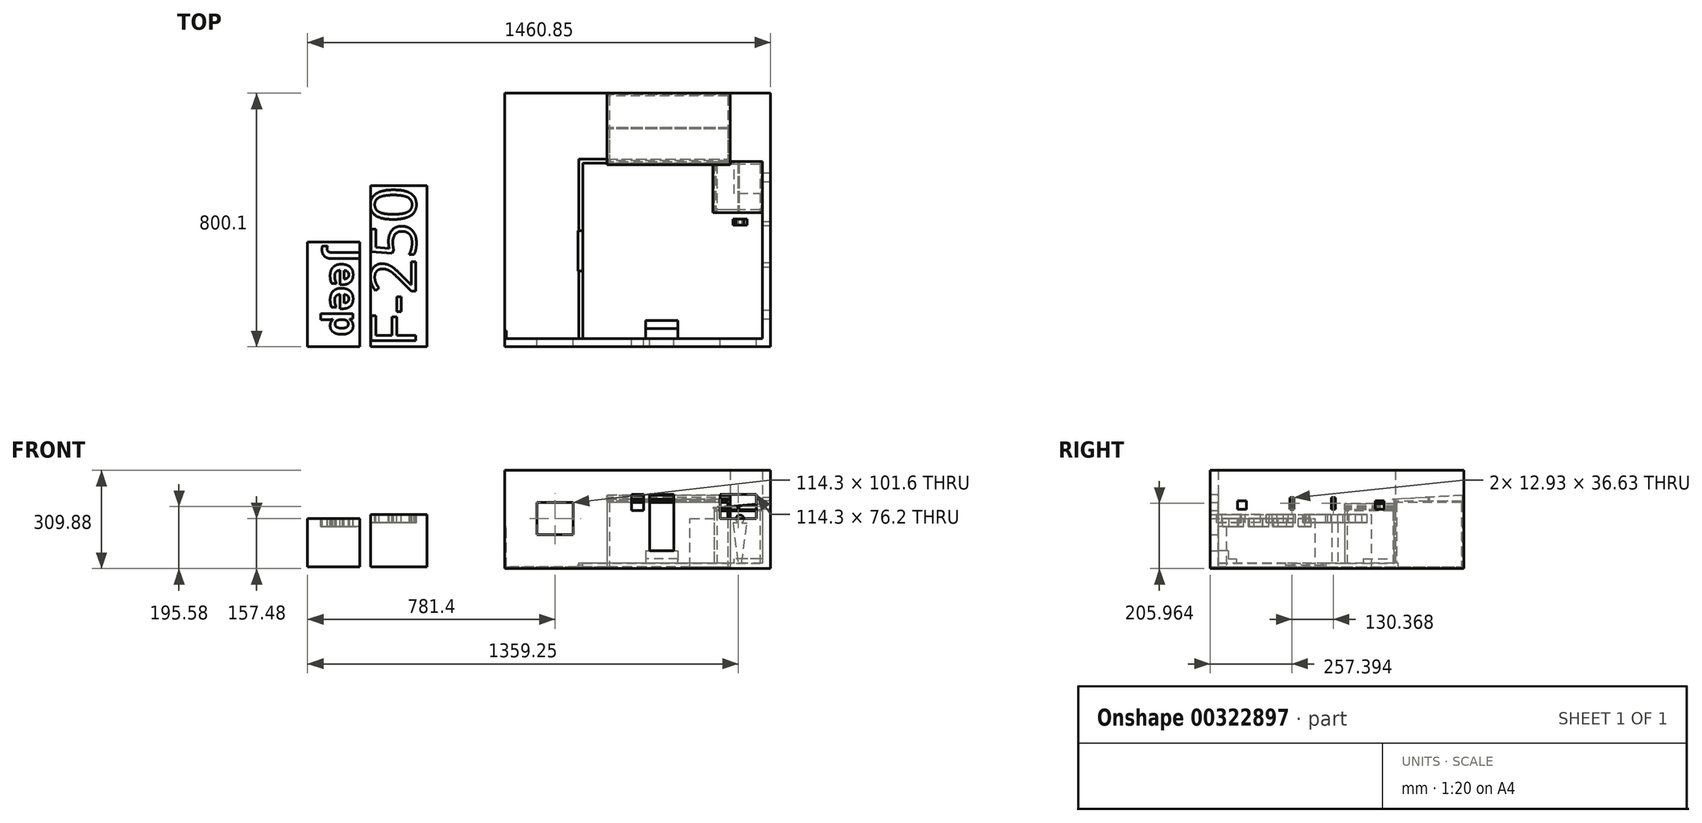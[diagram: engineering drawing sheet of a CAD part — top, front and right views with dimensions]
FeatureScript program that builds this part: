
annotation { "Feature Type Name" : "Feature", "Feature Type Description" : "" }
export const myFeature = defineFeature(function(context is Context, id is Id, definition is map)
    precondition{}
    {
        {
            var Q0;
            Q0=qCreatedBy(makeId("Top.planeOp"),FACE);
            var sketch = newSketch(context, id + "F0", { "sketchPlane" : qUnion([Q0])});
            skLineSegment(sketch, "E0.bottom", {"start": v(0, 0) * mm, "end": v(146.74, 0) * mm});
            skLineSegment(sketch, "E0.top", {"start": v(25.4, 25.4) * mm, "end": v(812.8, 25.4) * mm});
            skLineSegment(sketch, "E0.left", {"start": v(0, 0) * mm, "end": v(0, 25.4) * mm});
            skLineSegment(sketch, "E1.right", {"start": v(838.2, 25.4) * mm, "end": v(838.2, 584.2) * mm});
            skLineSegment(sketch, "E2", {"start": v(0, 25.4) * mm, "end": v(25.4, 25.4) * mm});
            skLineSegment(sketch, "E3", {"start": v(146.74, 0) * mm, "end": v(838.2, 0) * mm});
            skLineSegment(sketch, "E4", {"start": v(838.2, 0) * mm, "end": v(838.2, 25.4) * mm});
            skLineSegment(sketch, "E5.left", {"start": v(838.2, 584.2) * mm, "end": v(838.2, 192.84) * mm});
            skLineSegment(sketch, "E5.right", {"start": v(812.8, 584.2) * mm, "end": v(812.8, 25.4) * mm});
            skLineSegment(sketch, "E6.bottom", {"start": v(812.8, 584.2) * mm, "end": v(711.2, 584.2) * mm});
            skLineSegment(sketch, "E6.top", {"start": v(838.2, 800.1) * mm, "end": v(711.2, 800.1) * mm});
            skLineSegment(sketch, "E6.left", {"start": v(838.2, 584.2) * mm, "end": v(838.2, 800.1) * mm});
            skLineSegment(sketch, "E6.right", {"start": v(711.2, 584.2) * mm, "end": v(711.2, 800.1) * mm});
            skSolve(sketch);
        }
        {
            var Q0;
            Q0 = qSketchRegion(id + "F0", true);
            extrude(context, id + "F1", {"entities" : qUnion([Q0]), "depth" : 304.8 * mm});
        }
        {
            var Q0;
            Q0=makeQuery(id+"F1.opExtrude","SWEPT_FACE",FACE,{"disambiguationData":[OSD([sQuery(id+"F0.wireOp",EDGE,"E6.right")])]});
            var sketch = newSketch(context, id + "F2", { "sketchPlane" : qUnion([Q0])});
            skLineSegment(sketch, "E7.bottom", {"start": v(-800.1, 0) * mm, "end": v(-795.02, 0) * mm});
            skLineSegment(sketch, "E7.top", {"start": v(-800.1, 152.4) * mm, "end": v(-795.02, 152.4) * mm});
            skLineSegment(sketch, "E7.left", {"start": v(-800.1, 0) * mm, "end": v(-800.1, 152.4) * mm});
            skLineSegment(sketch, "E7.right", {"start": v(-795.02, 0) * mm, "end": v(-795.02, 152.4) * mm});
            skSolve(sketch);
        }
        {
            var Q0;
            Q0 = qSketchRegion(id + "F2", true);
            extrude(context, id + "F3", {"entities" : qUnion([Q0]), "operationType" : NewBodyOperationType.ADD, "depth" : 127 * mm});
        }
        {
            var Q0;
            Q0=makeQuery(id+"F1.opExtrude","SWEPT_FACE",FACE,{"disambiguationData":[OSD([sQuery(id+"F0.wireOp",EDGE,"E0.top"),sQuery(id+"F0.wireOp",EDGE,"E2")])]});
            var sketch = newSketch(context, id + "F4", { "sketchPlane" : qUnion([Q0])});
            skLineSegment(sketch, "E8.bottom", {"start": v(-101.6, 101.6) * mm, "end": v(-215.9, 101.6) * mm});
            skLineSegment(sketch, "E8.top", {"start": v(-101.6, 203.2) * mm, "end": v(-215.9, 203.2) * mm});
            skLineSegment(sketch, "E8.left", {"start": v(-101.6, 101.6) * mm, "end": v(-101.6, 203.2) * mm});
            skLineSegment(sketch, "E8.right", {"start": v(-215.9, 101.6) * mm, "end": v(-215.9, 203.2) * mm});
            skLineSegment(sketch, "E9.bottom", {"start": v(-400.05, 177.8) * mm, "end": v(-438.15, 177.8) * mm});
            skLineSegment(sketch, "E9.top", {"start": v(-400.05, 228.6) * mm, "end": v(-438.15, 228.6) * mm});
            skLineSegment(sketch, "E9.left", {"start": v(-400.05, 177.8) * mm, "end": v(-400.05, 228.6) * mm});
            skLineSegment(sketch, "E9.right", {"start": v(-438.15, 177.8) * mm, "end": v(-438.15, 228.6) * mm});
            skLineSegment(sketch, "E10.bottom", {"start": v(-679.45, 228.6) * mm, "end": v(-793.75, 228.6) * mm});
            skLineSegment(sketch, "E10.top", {"start": v(-679.45, 152.4) * mm, "end": v(-793.75, 152.4) * mm});
            skLineSegment(sketch, "E10.left", {"start": v(-679.45, 228.6) * mm, "end": v(-679.45, 152.4) * mm});
            skLineSegment(sketch, "E10.right", {"start": v(-793.75, 228.6) * mm, "end": v(-793.75, 152.4) * mm});
            skLineSegment(sketch, "E11.bottom", {"start": v(-457.2, 228.6) * mm, "end": v(-533.4, 228.6) * mm});
            skLineSegment(sketch, "E11.top", {"start": v(-457.2, 50.8) * mm, "end": v(-533.4, 50.8) * mm});
            skLineSegment(sketch, "E11.left", {"start": v(-457.2, 228.6) * mm, "end": v(-457.2, 50.8) * mm});
            skLineSegment(sketch, "E11.right", {"start": v(-533.4, 228.6) * mm, "end": v(-533.4, 50.8) * mm});
            skSolve(sketch);
        }
        {
            var Q0;
            Q0 = qSketchRegion(id + "F4", true);
            extrude(context, id + "F5", {"entities" : qUnion([Q0]), "operationType" : NewBodyOperationType.REMOVE, "endBound" : BoundingType.UP_TO_NEXT, "oppositeDirection" : true, "depth" : 25.4 * mm});
        }
        {
            var Q0;
            Q0=makeQuery(id+"F1.opExtrude","SWEPT_FACE",FACE,{"disambiguationData":[OSD([sQuery(id+"F0.wireOp",EDGE,"E0.top"),sQuery(id+"F0.wireOp",EDGE,"E2")])]});
            var sketch = newSketch(context, id + "F6", { "sketchPlane" : qUnion([Q0])});
            skLineSegment(sketch, "E12.bottom", {"start": v(-444.5, 50.8) * mm, "end": v(-546.1, 50.8) * mm});
            skLineSegment(sketch, "E12.top", {"start": v(-444.5, 0) * mm, "end": v(-546.1, 0) * mm});
            skLineSegment(sketch, "E12.left", {"start": v(-444.5, 50.8) * mm, "end": v(-444.5, 0) * mm});
            skLineSegment(sketch, "E12.right", {"start": v(-546.1, 50.8) * mm, "end": v(-546.1, 0) * mm});
            skSolve(sketch);
        }
        {
            var Q0;
            Q0 = qSketchRegion(id + "F6", true);
            extrude(context, id + "F7", {"entities" : qUnion([Q0]), "operationType" : NewBodyOperationType.ADD, "depth" : 31.75 * mm});
        }
        {
            var Q0;
            Q0=makeQuery(id+"F7.opExtrude","SWEPT_FACE",FACE,{"disambiguationData":[OSD([sQuery(id+"F6.wireOp",EDGE,"E12.left")])]});
            var sketch = newSketch(context, id + "F8", { "sketchPlane" : qUnion([Q0])});
            skLineSegment(sketch, "E13.bottom", {"start": v(-57.15, 25.4) * mm, "end": v(-82.55, 25.4) * mm});
            skLineSegment(sketch, "E13.top", {"start": v(-57.15, 0) * mm, "end": v(-82.55, 0) * mm});
            skLineSegment(sketch, "E13.left", {"start": v(-57.15, 25.4) * mm, "end": v(-57.15, 0) * mm});
            skLineSegment(sketch, "E13.right", {"start": v(-82.55, 25.4) * mm, "end": v(-82.55, 0) * mm});
            skSolve(sketch);
        }
        {
            var Q0;
            Q0 = qSketchRegion(id + "F8", true);
            var Q1;
            Q1=makeQuery(id+"F7.opExtrude","SWEPT_FACE",FACE,{"disambiguationData":[OSD([sQuery(id+"F6.wireOp",EDGE,"E12.right")])]});
            extrude(context, id + "F9", {"entities" : qUnion([Q0]), "operationType" : NewBodyOperationType.ADD, "endBound" : BoundingType.UP_TO_SURFACE, "oppositeDirection" : true, "endBoundEntityFace" : qUnion([Q1]), "depth" : 25.4 * mm});
        }
        {
            var Q0;
            Q0=makeQuery(id+"F1.opExtrude","SWEPT_FACE",FACE,{"disambiguationData":[OSD([sQuery(id+"F0.wireOp",EDGE,"E0.top"),sQuery(id+"F0.wireOp",EDGE,"E2")])]});
            var sketch = newSketch(context, id + "F10", { "sketchPlane" : qUnion([Q0])});
            skLineSegment(sketch, "E14.bottom", {"start": v(0, 0) * mm, "end": v(-5.08, 0) * mm});
            skLineSegment(sketch, "E14.top", {"start": v(0, 127) * mm, "end": v(-5.08, 127) * mm});
            skLineSegment(sketch, "E14.left", {"start": v(0, 0) * mm, "end": v(0, 127) * mm});
            skLineSegment(sketch, "E14.right", {"start": v(-5.08, 0) * mm, "end": v(-5.08, 127) * mm});
            skSolve(sketch);
        }
        {
            var Q0;
            Q0 = qSketchRegion(id + "F10", true);
            extrude(context, id + "F11", {"entities" : qUnion([Q0]), "operationType" : NewBodyOperationType.ADD, "depth" : 25.4 * mm});
        }
        {
            var Q0;
            Q0=makeQuery(id+"F11.boolean.opBoolean","MERGE",FACE,{"derivedFrom":[makeQuery(id+"F9.boolean.opBoolean","MERGE",FACE,{"derivedFrom":[makeQuery(id+"F7.boolean.opBoolean","MERGE",FACE,{"derivedFrom":[makeQuery(id+"F3.boolean.opBoolean","MERGE",FACE,{"derivedFrom":[makeQuery(id+"F1.opExtrude","CAP_FACE",FACE,{"disambiguationData":[OSD([sQuery(id+"F0.wireOp",EDGE,"E0.bottom"),sQuery(id+"F0.wireOp",EDGE,"E0.top"),sQuery(id+"F0.wireOp",EDGE,"E0.left"),sQuery(id+"F0.wireOp",EDGE,"E1.right"),sQuery(id+"F0.wireOp",EDGE,"E2"),sQuery(id+"F0.wireOp",EDGE,"E3"),sQuery(id+"F0.wireOp",EDGE,"E4"),sQuery(id+"F0.wireOp",EDGE,"E5.left"),sQuery(id+"F0.wireOp",EDGE,"E5.right"),sQuery(id+"F0.wireOp",EDGE,"E6.bottom"),sQuery(id+"F0.wireOp",EDGE,"E6.top"),sQuery(id+"F0.wireOp",EDGE,"E6.left"),sQuery(id+"F0.wireOp",EDGE,"E6.right")])],"isStart":true}),makeQuery(id+"F3.opExtrude","SWEPT_FACE",FACE,{"disambiguationData":[OSD([sQuery(id+"F2.wireOp",EDGE,"E7.bottom")])]})]}),makeQuery(id+"F7.opExtrude","SWEPT_FACE",FACE,{"disambiguationData":[OSD([sQuery(id+"F6.wireOp",EDGE,"E12.top")])]})]}),makeQuery(id+"F9.opExtrude","SWEPT_FACE",FACE,{"disambiguationData":[OSD([sQuery(id+"F8.wireOp",EDGE,"E13.top")])]})]}),makeQuery(id+"F11.opExtrude","SWEPT_FACE",FACE,{"disambiguationData":[OSD([sQuery(id+"F10.wireOp",EDGE,"E14.bottom")])]})]});
            var sketch = newSketch(context, id + "F12", { "sketchPlane" : qUnion([Q0])});
            skLineSegment(sketch, "E15.bottom", {"start": v(0, 0) * mm, "end": v(838.2, 0) * mm});
            skLineSegment(sketch, "E15.top", {"start": v(0, -800.1) * mm, "end": v(838.2, -800.1) * mm});
            skLineSegment(sketch, "E15.left", {"start": v(0, 0) * mm, "end": v(0, -800.1) * mm});
            skLineSegment(sketch, "E15.right", {"start": v(838.2, 0) * mm, "end": v(838.2, -800.1) * mm});
            skSolve(sketch);
        }
        {
            var Q0;
            Q0 = qSketchRegion(id + "F12", true);
            extrude(context, id + "F13", {"entities" : qUnion([Q0]), "operationType" : NewBodyOperationType.ADD, "depth" : 5.08 * mm});
        }
        {
            var Q0;
            Q0=makeQuery(id+"F1.opExtrude","SWEPT_FACE",FACE,{"disambiguationData":[OSD([sQuery(id+"F0.wireOp",EDGE,"E6.bottom")])]});
            var sketch = newSketch(context, id + "F14", { "sketchPlane" : qUnion([Q0])});
            skLineSegment(sketch, "E16.bottom", {"start": v(812.8, 0) * mm, "end": v(723.9, 0) * mm});
            skLineSegment(sketch, "E16.top", {"start": v(812.8, 25.4) * mm, "end": v(723.9, 25.4) * mm});
            skLineSegment(sketch, "E16.left", {"start": v(812.8, 0) * mm, "end": v(812.8, 25.4) * mm});
            skLineSegment(sketch, "E16.right", {"start": v(723.9, 0) * mm, "end": v(723.9, 25.4) * mm});
            skSolve(sketch);
        }
        {
            var Q0;
            Q0 = qSketchRegion(id + "F14", true);
            extrude(context, id + "F15", {"entities" : qUnion([Q0]), "operationType" : NewBodyOperationType.ADD, "depth" : 101.6 * mm});
        }
        {
            var Q0;
            Q0=makeQuery(id+"F13.opExtrude","CAP_FACE",FACE,{"disambiguationData":[OSD([sQuery(id+"F12.wireOp",EDGE,"E15.bottom"),sQuery(id+"F12.wireOp",EDGE,"E15.top"),sQuery(id+"F12.wireOp",EDGE,"E15.left"),sQuery(id+"F12.wireOp",EDGE,"E15.right")])],"isStart":true});
            var sketch = newSketch(context, id + "F16", { "sketchPlane" : qUnion([Q0])});
            skLineSegment(sketch, "E17", {"start": v(233.68, 25.4) * mm, "end": v(233.68, 591.82) * mm});
            skLineSegment(sketch, "E18", {"start": v(233.68, 591.82) * mm, "end": v(711.2, 591.82) * mm});
            skLineSegment(sketch, "E19.0", {"start": v(246.38, 579.12) * mm, "end": v(406.4, 579.12) * mm});
            skLineSegment(sketch, "E19.1", {"start": v(246.38, 25.4) * mm, "end": v(246.38, 579.12) * mm});
            skLineSegment(sketch, "E20", {"start": v(246.38, 25.4) * mm, "end": v(233.68, 25.4) * mm});
            skLineSegment(sketch, "E21.bottom", {"start": v(711.2, 591.82) * mm, "end": v(812.8, 591.82) * mm});
            skLineSegment(sketch, "E21.top", {"start": v(406.4, 579.12) * mm, "end": v(812.8, 579.12) * mm});
            skLineSegment(sketch, "E21.right", {"start": v(812.8, 591.82) * mm, "end": v(812.8, 579.12) * mm});
            skSolve(sketch);
        }
        {
            var Q0;
            Q0 = qSketchRegion(id + "F16", true);
            extrude(context, id + "F17", {"entities" : qUnion([Q0]), "operationType" : NewBodyOperationType.ADD, "depth" : 12.7 * mm});
        }
        {
            var Q0;
            Q0=makeQuery(id+"F1.opExtrude","SWEPT_FACE",FACE,{"disambiguationData":[OSD([sQuery(id+"F0.wireOp",EDGE,"E5.right")])]});
            var sketch = newSketch(context, id + "F18", { "sketchPlane" : qUnion([Q0])});
            skLineSegment(sketch, "E22.bottom", {"start": v(-114.1, 208.43) * mm, "end": v(-86.08, 208.43) * mm});
            skLineSegment(sketch, "E22.top", {"start": v(-114.1, 181.5) * mm, "end": v(-86.08, 181.5) * mm});
            skLineSegment(sketch, "E22.left", {"start": v(-114.1, 208.43) * mm, "end": v(-114.1, 181.5) * mm});
            skLineSegment(sketch, "E22.right", {"start": v(-86.08, 208.43) * mm, "end": v(-86.08, 181.5) * mm});
            skPoint(sketch, "E23.oppositeSnap0", {"position": v(-100.1, 181.5) * mm});
            skLineSegment(sketch, "E23.bottom", {"start": v(-548.3, 208.43) * mm, "end": v(-520.28, 208.43) * mm});
            skLineSegment(sketch, "E23.top", {"start": v(-548.3, 181.5) * mm, "end": v(-520.28, 181.5) * mm});
            skLineSegment(sketch, "E23.left", {"start": v(-548.3, 208.43) * mm, "end": v(-548.3, 181.5) * mm});
            skLineSegment(sketch, "E23.right", {"start": v(-520.28, 208.43) * mm, "end": v(-520.28, 181.5) * mm});
            skLineSegment(sketch, "E24.bottom", {"start": v(-394.23, 219.2) * mm, "end": v(-381.3, 219.2) * mm});
            skLineSegment(sketch, "E24.top", {"start": v(-394.23, 182.57) * mm, "end": v(-381.3, 182.57) * mm});
            skLineSegment(sketch, "E24.left", {"start": v(-394.23, 219.2) * mm, "end": v(-394.23, 182.57) * mm});
            skLineSegment(sketch, "E24.right", {"start": v(-381.3, 219.2) * mm, "end": v(-381.3, 182.57) * mm});
            skLineSegment(sketch, "E25.bottom", {"start": v(-263.86, 219.2) * mm, "end": v(-250.93, 219.2) * mm});
            skLineSegment(sketch, "E25.top", {"start": v(-263.86, 182.57) * mm, "end": v(-250.93, 182.57) * mm});
            skLineSegment(sketch, "E25.left", {"start": v(-263.86, 219.2) * mm, "end": v(-263.86, 182.57) * mm});
            skLineSegment(sketch, "E25.right", {"start": v(-250.93, 219.2) * mm, "end": v(-250.93, 182.57) * mm});
            skSolve(sketch);
        }
        {
            var Q0;
            Q0 = qSketchRegion(id + "F18", true);
            var Q1;
            Q1=makeQuery(id+"F13.boolean.opBoolean","MERGE",FACE,{"derivedFrom":[makeQuery(id+"F1.opExtrude","SWEPT_FACE",FACE,{"disambiguationData":[OSD([sQuery(id+"F0.wireOp",EDGE,"E1.right"),sQuery(id+"F0.wireOp",EDGE,"E4"),sQuery(id+"F0.wireOp",EDGE,"E5.left"),sQuery(id+"F0.wireOp",EDGE,"E6.left")])]}),makeQuery(id+"F13.opExtrude","SWEPT_FACE",FACE,{"disambiguationData":[OSD([sQuery(id+"F12.wireOp",EDGE,"E15.right")])]})]});
            extrude(context, id + "F19", {"entities" : qUnion([Q0]), "operationType" : NewBodyOperationType.REMOVE, "endBound" : BoundingType.UP_TO_SURFACE, "oppositeDirection" : true, "endBoundEntityFace" : qUnion([Q1]), "depth" : 25.4 * mm});
        }
        {
            var Q0;
            Q0=qCreatedBy(makeId("Top.planeOp"),FACE);
            var sketch = newSketch(context, id + "F20", { "sketchPlane" : qUnion([Q0])});
            skLineSegment(sketch, "E26.bottom", {"start": v(-622.65, 0) * mm, "end": v(-457.55, 0) * mm});
            skLineSegment(sketch, "E26.top", {"start": v(-622.65, 330.2) * mm, "end": v(-457.55, 330.2) * mm});
            skLineSegment(sketch, "E26.left", {"start": v(-622.65, 0) * mm, "end": v(-622.65, 330.2) * mm});
            skLineSegment(sketch, "E26.right", {"start": v(-457.55, 0) * mm, "end": v(-457.55, 330.2) * mm});
            skSolve(sketch);
        }
        {
            var Q0;
            Q0 = qSketchRegion(id + "F20", true);
            extrude(context, id + "F21", {"entities" : qUnion([Q0]), "depth" : 152.4 * mm});
        }
        {
            var Q0;
            Q0=makeQuery(id+"F21.opExtrude","CAP_FACE",FACE,{"disambiguationData":[OSD([sQuery(id+"F20.wireOp",EDGE,"E26.bottom"),sQuery(id+"F20.wireOp",EDGE,"E26.top"),sQuery(id+"F20.wireOp",EDGE,"E26.left"),sQuery(id+"F20.wireOp",EDGE,"E26.right")])],"isStart":false});
            var sketch = newSketch(context, id + "F22", { "sketchPlane" : qUnion([Q0])});
            skText(sketch, "E27", { "text": "Jeep", "fontName": "OpenSans-Bold.ttf"});
            const initialGuessF22  = {"E27": [-0.54998, 0.30887, 0, -1, 0.09243]};
            skSetInitialGuess(sketch, initialGuessF22);
            skSolve(sketch);
        }
        {
            var Q0;
            Q0 = qSketchRegion(id + "F22", true);
            extrude(context, id + "F23", {"entities" : qUnion([Q0]), "operationType" : NewBodyOperationType.REMOVE, "oppositeDirection" : true, "depth" : 25.4 * mm});
        }
        {
            var Q0;
            Q0=qCreatedBy(makeId("Top.planeOp"),FACE);
            var sketch = newSketch(context, id + "F24", { "sketchPlane" : qUnion([Q0])});
            skLineSegment(sketch, "E28.bottom", {"start": v(-245.53, 0) * mm, "end": v(-423.33, 0) * mm});
            skLineSegment(sketch, "E28.top", {"start": v(-245.53, 508) * mm, "end": v(-423.33, 508) * mm});
            skLineSegment(sketch, "E28.left", {"start": v(-245.53, 0) * mm, "end": v(-245.53, 508) * mm});
            skLineSegment(sketch, "E28.right", {"start": v(-423.33, 0) * mm, "end": v(-423.33, 508) * mm});
            skSolve(sketch);
        }
        {
            var Q0;
            Q0 = qSketchRegion(id + "F24", true);
            extrude(context, id + "F25", {"entities" : qUnion([Q0]), "depth" : 165.1 * mm});
        }
        {
            var Q0;
            Q0=makeQuery(id+"F25.opExtrude","CAP_FACE",FACE,{"disambiguationData":[OSD([sQuery(id+"F24.wireOp",EDGE,"E28.bottom"),sQuery(id+"F24.wireOp",EDGE,"E28.top"),sQuery(id+"F24.wireOp",EDGE,"E28.left"),sQuery(id+"F24.wireOp",EDGE,"E28.right")])],"isStart":false});
            var sketch = newSketch(context, id + "F26", { "sketchPlane" : qUnion([Q0])});
            skText(sketch, "E29", { "text": "F-250\n", "fontName": "OpenSans-Regular.ttf"});
            const initialGuessF26  = {"E29": [-0.28091, 0, 0, 1, 0.14242]};
            skSetInitialGuess(sketch, initialGuessF26);
            skSolve(sketch);
        }
        {
            var Q0;
            Q0 = qSketchRegion(id + "F26", true);
            extrude(context, id + "F27", {"entities" : qUnion([Q0]), "operationType" : NewBodyOperationType.REMOVE, "oppositeDirection" : true, "depth" : 25.4 * mm});
        }
        {
            var Q0;
            Q0=makeQuery(id+"F17.boolean.opBoolean","SPLIT",FACE,{"disambiguationData":[TD([makeQuery(id+"F1.opExtrude","SWEPT_FACE",FACE,{"disambiguationData":[OSD([sQuery(id+"F0.wireOp",EDGE,"E5.right")])]})])],"derivedFrom":makeQuery(id+"F13.opExtrude","CAP_FACE",FACE,{"disambiguationData":[OSD([sQuery(id+"F12.wireOp",EDGE,"E15.bottom"),sQuery(id+"F12.wireOp",EDGE,"E15.top"),sQuery(id+"F12.wireOp",EDGE,"E15.left"),sQuery(id+"F12.wireOp",EDGE,"E15.right")])],"isStart":true})});
            cPlane(context, id + "F28", {"entities" : qUnion([Q0]), "cplaneType" : CPlaneType.OFFSET, "offset" : 0 * mm, "width" : 152.4 * mm, "height" : 152.4 * mm});
        }
        {
            var Q0;
            Q0=qCreatedBy(id+"F28.planeOp",FACE);
            var sketch = newSketch(context, id + "F29", { "sketchPlane" : qUnion([Q0])});
            skLineSegment(sketch, "E30.0.0", {"start": v(723.9, 579.12) * mm, "end": v(246.38, 579.12) * mm});
            skLineSegment(sketch, "E30.0.1", {"start": v(246.38, 579.12) * mm, "end": v(246.38, 25.4) * mm});
            skLineSegment(sketch, "E30.0.2", {"start": v(246.38, 25.4) * mm, "end": v(444.5, 25.4) * mm});
            skLineSegment(sketch, "E30.0.3", {"start": v(444.5, 25.4) * mm, "end": v(444.5, 82.55) * mm});
            skLineSegment(sketch, "E30.0.4", {"start": v(444.5, 82.55) * mm, "end": v(546.1, 82.55) * mm});
            skLineSegment(sketch, "E30.0.5", {"start": v(546.1, 82.55) * mm, "end": v(546.1, 25.4) * mm});
            skLineSegment(sketch, "E30.0.6", {"start": v(546.1, 25.4) * mm, "end": v(812.8, 25.4) * mm});
            skLineSegment(sketch, "E30.0.7", {"start": v(812.8, 25.4) * mm, "end": v(812.8, 482.6) * mm});
            skLineSegment(sketch, "E30.0.8", {"start": v(812.8, 482.6) * mm, "end": v(723.9, 482.6) * mm});
            skLineSegment(sketch, "E30.0.9", {"start": v(723.9, 482.6) * mm, "end": v(723.9, 579.12) * mm});
            skSolve(sketch);
        }
        {
            var Q0;
            Q0 = qSketchRegion(id + "F29", true);
            extrude(context, id + "F30", {"entities" : qUnion([Q0]), "depth" : 11.43 * mm});
        }
        {
            var Q0;
            Q0=makeQuery(id+"F17.opExtrude","CAP_FACE",FACE,{"disambiguationData":[OSD([sQuery(id+"F16.wireOp",EDGE,"E17"),sQuery(id+"F16.wireOp",EDGE,"E18"),sQuery(id+"F16.wireOp",EDGE,"E19.0"),sQuery(id+"F16.wireOp",EDGE,"E19.1"),sQuery(id+"F16.wireOp",EDGE,"E20"),sQuery(id+"F16.wireOp",EDGE,"E21.bottom"),sQuery(id+"F16.wireOp",EDGE,"E21.top"),sQuery(id+"F16.wireOp",EDGE,"E21.right")])],"isStart":false});
            var sketch = newSketch(context, id + "F31", { "sketchPlane" : qUnion([Q0])});
            skLineSegment(sketch, "E31.bottom", {"start": v(233.68, 238.76) * mm, "end": v(246.38, 238.76) * mm});
            skLineSegment(sketch, "E31.top", {"start": v(233.68, 365.76) * mm, "end": v(246.38, 365.76) * mm});
            skLineSegment(sketch, "E31.left", {"start": v(233.68, 238.76) * mm, "end": v(233.68, 365.76) * mm});
            skPoint(sketch, "E31.middle", {"position": v(246.38, 302.26) * mm});
            skLineSegment(sketch, "E32", {"start": v(246.38, 365.76) * mm, "end": v(246.38, 238.76) * mm});
            skSolve(sketch);
        }
        {
            var Q0;
            Q0 = qSketchRegion(id + "F31", true);
            extrude(context, id + "F32", {"entities" : qUnion([Q0]), "operationType" : NewBodyOperationType.REMOVE, "oppositeDirection" : true, "depth" : 12.7 * mm});
        }
        {
            var Q0;
            Q0=makeQuery(id+"F30.opExtrude","SWEPT_FACE",FACE,{"disambiguationData":[OSD([sQuery(id+"F29.wireOp",EDGE,"E30.0.1")])]});
            var sketch = newSketch(context, id + "F33", { "sketchPlane" : qUnion([Q0])});
            skLineSegment(sketch, "E33.bottom", {"start": v(-238.74, 0) * mm, "end": v(-365.78, 0) * mm});
            skLineSegment(sketch, "E33.top", {"start": v(-238.74, 6.35) * mm, "end": v(-365.78, 6.35) * mm});
            skLineSegment(sketch, "E33.left", {"start": v(-238.74, 0) * mm, "end": v(-238.74, 6.35) * mm});
            skLineSegment(sketch, "E33.right", {"start": v(-365.78, 0) * mm, "end": v(-365.78, 6.35) * mm});
            skPoint(sketch, "E33.middle", {"position": v(-302.26, 3.17) * mm});
            skPoint(sketch, "E33.middle.positionSnap0", {"position": v(-302.26, 11.43) * mm});
            skPoint(sketch, "E33.centerSnap0", {"position": v(-302.26, 11.43) * mm});
            skSolve(sketch);
        }
        {
            var Q0;
            Q0 = qSketchRegion(id + "F33", true);
            extrude(context, id + "F34", {"entities" : qUnion([Q0]), "depth" : 15.24 * mm});
        }
        {
            var Q0;
            Q0=makeQuery(id+"F30.opExtrude","CAP_FACE",FACE,{"disambiguationData":[OSD([sQuery(id+"F29.wireOp",EDGE,"E30.0.0"),sQuery(id+"F29.wireOp",EDGE,"E30.0.1"),sQuery(id+"F29.wireOp",EDGE,"E30.0.2"),sQuery(id+"F29.wireOp",EDGE,"E30.0.3"),sQuery(id+"F29.wireOp",EDGE,"E30.0.4"),sQuery(id+"F29.wireOp",EDGE,"E30.0.5"),sQuery(id+"F29.wireOp",EDGE,"E30.0.6"),sQuery(id+"F29.wireOp",EDGE,"E30.0.7"),sQuery(id+"F29.wireOp",EDGE,"E30.0.8"),sQuery(id+"F29.wireOp",EDGE,"E30.0.9")])],"isStart":false});
            var sketch = newSketch(context, id + "F35", { "sketchPlane" : qUnion([Q0])});
            skLineSegment(sketch, "E34.bottom", {"start": v(660.4, 575.74) * mm, "end": v(668.86, 575.74) * mm});
            skLineSegment(sketch, "E34.top", {"start": v(660.4, 584.2) * mm, "end": v(668.86, 584.2) * mm});
            skLineSegment(sketch, "E34.left", {"start": v(660.4, 575.74) * mm, "end": v(660.4, 584.2) * mm});
            skLineSegment(sketch, "E34.right", {"start": v(668.86, 575.74) * mm, "end": v(668.86, 584.2) * mm});
            skLineSegment(sketch, "E35.bottom", {"start": v(812.8, 584.2) * mm, "end": v(804.34, 584.2) * mm});
            skLineSegment(sketch, "E35.top", {"start": v(812.8, 575.74) * mm, "end": v(804.34, 575.74) * mm});
            skLineSegment(sketch, "E35.left", {"start": v(812.8, 584.2) * mm, "end": v(812.8, 575.74) * mm});
            skLineSegment(sketch, "E35.right", {"start": v(804.34, 584.2) * mm, "end": v(804.34, 575.74) * mm});
            skLineSegment(sketch, "E36.0.1.0", {"start": v(660.4, 423.34) * mm, "end": v(660.4, 431.8) * mm});
            skLineSegment(sketch, "E36.0.1.1", {"start": v(660.4, 431.8) * mm, "end": v(668.86, 431.8) * mm});
            skLineSegment(sketch, "E36.0.1.2", {"start": v(660.4, 423.34) * mm, "end": v(668.86, 423.34) * mm});
            skLineSegment(sketch, "E36.0.1.3", {"start": v(668.86, 423.34) * mm, "end": v(668.86, 431.8) * mm});
            skLineSegment(sketch, "E36.0.1.4", {"start": v(812.8, 423.34) * mm, "end": v(804.34, 423.34) * mm});
            skLineSegment(sketch, "E36.0.1.5", {"start": v(804.34, 431.8) * mm, "end": v(804.34, 423.34) * mm});
            skLineSegment(sketch, "E36.0.1.6", {"start": v(812.8, 431.8) * mm, "end": v(812.8, 423.34) * mm});
            skLineSegment(sketch, "E36.0.1.7", {"start": v(812.8, 431.8) * mm, "end": v(804.34, 431.8) * mm});
            skLineSegment(sketch, "E36.direction1", {"start": v(660.4, 575.74) * mm, "end": v(715.44, 575.74) * mm, "construction": true});
            skLineSegment(sketch, "E36.direction2", {"start": v(660.4, 575.74) * mm, "end": v(660.4, 423.34) * mm, "construction": true});
            skSolve(sketch);
        }
        {
            var Q0;
            Q0=makeQuery(id+"F30.opExtrude","CAP_FACE",FACE,{"disambiguationData":[OSD([sQuery(id+"F29.wireOp",EDGE,"E30.0.0"),sQuery(id+"F29.wireOp",EDGE,"E30.0.1"),sQuery(id+"F29.wireOp",EDGE,"E30.0.2"),sQuery(id+"F29.wireOp",EDGE,"E30.0.3"),sQuery(id+"F29.wireOp",EDGE,"E30.0.4"),sQuery(id+"F29.wireOp",EDGE,"E30.0.5"),sQuery(id+"F29.wireOp",EDGE,"E30.0.6"),sQuery(id+"F29.wireOp",EDGE,"E30.0.7"),sQuery(id+"F29.wireOp",EDGE,"E30.0.8"),sQuery(id+"F29.wireOp",EDGE,"E30.0.9")])],"isStart":false});
            var sketch = newSketch(context, id + "F36", { "sketchPlane" : qUnion([Q0])});
            skPoint(sketch, "E37.0", {"position": v(812.8, 423.34) * mm});
            skPoint(sketch, "E38.0", {"position": v(812.8, 584.2) * mm});
            skPoint(sketch, "E39.0", {"position": v(660.4, 584.2) * mm});
            skPoint(sketch, "E40.0", {"position": v(660.4, 423.34) * mm});
            skLineSegment(sketch, "E41.bottom", {"start": v(812.8, 584.2) * mm, "end": v(660.4, 584.2) * mm});
            skLineSegment(sketch, "E41.top", {"start": v(812.8, 423.34) * mm, "end": v(660.4, 423.34) * mm});
            skLineSegment(sketch, "E41.left", {"start": v(812.8, 584.2) * mm, "end": v(812.8, 423.34) * mm});
            skLineSegment(sketch, "E41.right", {"start": v(660.4, 584.2) * mm, "end": v(660.4, 423.34) * mm});
            skLineSegment(sketch, "E42.0", {"start": v(804.34, 575.74) * mm, "end": v(804.34, 431.8) * mm});
            skLineSegment(sketch, "E42.1", {"start": v(804.34, 575.74) * mm, "end": v(668.86, 575.74) * mm});
            skLineSegment(sketch, "E42.2", {"start": v(668.86, 575.74) * mm, "end": v(668.86, 431.8) * mm});
            skLineSegment(sketch, "E42.3", {"start": v(804.34, 431.8) * mm, "end": v(668.86, 431.8) * mm});
            skSolve(sketch);
        }
        {
            var Q0;
            Q0 = qSketchRegion(id + "F36", true);
            extrude(context, id + "F37", {"entities" : qUnion([Q0]), "depth" : 169.34 * mm, "hasSecondDirection" : true, "secondDirectionOppositeDirection" : false, "secondDirectionDepth" : 165.1 * mm});
        }
        {
            var Q0;
            Q0 = qSketchRegion(id + "F35", true);
            var Q1;
            Q1=makeQuery(id+"F37.opExtrude","CAP_FACE",FACE,{"disambiguationData":[OSD([sQuery(id+"F36.wireOp",EDGE,"E41.bottom"),sQuery(id+"F36.wireOp",EDGE,"E41.top"),sQuery(id+"F36.wireOp",EDGE,"E41.left"),sQuery(id+"F36.wireOp",EDGE,"E41.right"),sQuery(id+"F36.wireOp",EDGE,"E42.0"),sQuery(id+"F36.wireOp",EDGE,"E42.1"),sQuery(id+"F36.wireOp",EDGE,"E42.2"),sQuery(id+"F36.wireOp",EDGE,"E42.3")])],"isStart":true});
            extrude(context, id + "F38", {"entities" : qUnion([Q0]), "operationType" : NewBodyOperationType.ADD, "endBound" : BoundingType.UP_TO_SURFACE, "endBoundEntityFace" : qUnion([Q1]), "depth" : 165.1 * mm});
        }
        {
            var Q0;
            Q0=makeQuery(id+"F38.boolean.opBoolean","MERGE",FACE,{"derivedFrom":[makeQuery(id+"F37.opExtrude","SWEPT_FACE",FACE,{"disambiguationData":[OSD([sQuery(id+"F36.wireOp",EDGE,"E41.top")])]}),makeQuery(id+"F38.opExtrude","SWEPT_FACE",FACE,{"disambiguationData":[OSD([sQuery(id+"F35.wireOp",EDGE,"E36.0.1.2")])]}),makeQuery(id+"F38.opExtrude","SWEPT_FACE",FACE,{"disambiguationData":[OSD([sQuery(id+"F35.wireOp",EDGE,"E36.0.1.4")])]})]});
            var sketch = newSketch(context, id + "F39", { "sketchPlane" : qUnion([Q0])});
            skLineSegment(sketch, "E43", {"start": v(660.4, 180.77) * mm, "end": v(660.4, 186.2) * mm});
            skLineSegment(sketch, "E44", {"start": v(812.8, 180.77) * mm, "end": v(812.8, 199.82) * mm});
            skLineSegment(sketch, "E45", {"start": v(812.8, 199.82) * mm, "end": v(660.4, 187.27) * mm});
            skLineSegment(sketch, "E46.0", {"start": v(664.64, 180.77) * mm, "end": v(664.64, 186.56) * mm});
            skLineSegment(sketch, "E46.1", {"start": v(808.56, 198.4) * mm, "end": v(738.42, 192.63) * mm});
            skLineSegment(sketch, "E46.2", {"start": v(808.56, 180.77) * mm, "end": v(808.56, 198.4) * mm});
            skLineSegment(sketch, "E47", {"start": v(660.4, 186.2) * mm, "end": v(656.16, 185.86) * mm});
            skLineSegment(sketch, "E48", {"start": v(656.16, 185.86) * mm, "end": v(656.07, 186.91) * mm});
            skLineSegment(sketch, "E49", {"start": v(656.07, 186.91) * mm, "end": v(660.4, 187.27) * mm});
            skLineSegment(sketch, "E50.bottom", {"start": v(738.42, 180.77) * mm, "end": v(734.78, 180.77) * mm});
            skLineSegment(sketch, "E50.left", {"start": v(738.42, 180.77) * mm, "end": v(738.42, 192.63) * mm});
            skLineSegment(sketch, "E50.right", {"start": v(734.78, 180.77) * mm, "end": v(734.78, 192.33) * mm});
            skPoint(sketch, "E50.middle", {"position": v(736.6, 192.48) * mm});
            skLineSegment(sketch, "E51.trimOffspring", {"start": v(734.78, 192.33) * mm, "end": v(664.64, 186.56) * mm});
            skLineSegment(sketch, "E52", {"start": v(660.4, 180.77) * mm, "end": v(664.64, 180.77) * mm});
            skLineSegment(sketch, "E53", {"start": v(808.56, 180.77) * mm, "end": v(812.8, 180.77) * mm});
            skSolve(sketch);
        }
        {
            var Q0;
            Q0 = qSketchRegion(id + "F39", true);
            var Q1;
            Q1=makeQuery(id+"F38.boolean.opBoolean","MERGE",FACE,{"derivedFrom":[makeQuery(id+"F37.opExtrude","SWEPT_FACE",FACE,{"disambiguationData":[OSD([sQuery(id+"F36.wireOp",EDGE,"E41.bottom")])]}),makeQuery(id+"F38.opExtrude","SWEPT_FACE",FACE,{"disambiguationData":[OSD([sQuery(id+"F35.wireOp",EDGE,"E34.top")])]}),makeQuery(id+"F38.opExtrude","SWEPT_FACE",FACE,{"disambiguationData":[OSD([sQuery(id+"F35.wireOp",EDGE,"E35.bottom")])]})]});
            extrude(context, id + "F40", {"entities" : qUnion([Q0]), "operationType" : NewBodyOperationType.ADD, "endBound" : BoundingType.UP_TO_SURFACE, "oppositeDirection" : true, "endBoundEntityFace" : qUnion([Q1]), "depth" : 25.4 * mm});
        }
        {
            var Q0;
            Q0=makeQuery(id+"F30.opExtrude","CAP_FACE",FACE,{"disambiguationData":[OSD([sQuery(id+"F29.wireOp",EDGE,"E30.0.0"),sQuery(id+"F29.wireOp",EDGE,"E30.0.1"),sQuery(id+"F29.wireOp",EDGE,"E30.0.2"),sQuery(id+"F29.wireOp",EDGE,"E30.0.3"),sQuery(id+"F29.wireOp",EDGE,"E30.0.4"),sQuery(id+"F29.wireOp",EDGE,"E30.0.5"),sQuery(id+"F29.wireOp",EDGE,"E30.0.6"),sQuery(id+"F29.wireOp",EDGE,"E30.0.7"),sQuery(id+"F29.wireOp",EDGE,"E30.0.8"),sQuery(id+"F29.wireOp",EDGE,"E30.0.9")])],"isStart":false});
            var sketch = newSketch(context, id + "F41", { "sketchPlane" : qUnion([Q0])});
            skLineSegment(sketch, "E54.bottom", {"start": v(763.46, 402.5) * mm, "end": v(719, 402.5) * mm});
            skLineSegment(sketch, "E54.top", {"start": v(763.46, 383.46) * mm, "end": v(719, 383.46) * mm});
            skLineSegment(sketch, "E54.left", {"start": v(763.46, 402.5) * mm, "end": v(763.46, 383.46) * mm});
            skLineSegment(sketch, "E54.right", {"start": v(719, 402.5) * mm, "end": v(719, 383.46) * mm});
            skPoint(sketch, "E54.middle", {"position": v(741.23, 392.98) * mm});
            skSolve(sketch);
        }
        {
            var Q0;
            Q0 = qSketchRegion(id + "F41", true);
            extrude(context, id + "F42", {"entities" : qUnion([Q0]), "depth" : 152.4 * mm});
        }
        {
            var Q0;
            Q0=makeQuery(id+"F42.opExtrude","SWEPT_FACE",FACE,{"disambiguationData":[OSD([sQuery(id+"F41.wireOp",EDGE,"E54.top")])]});
            var sketch = newSketch(context, id + "F43", { "sketchPlane" : qUnion([Q0])});
            skArc(sketch, "E55", {"start": v(747.45, 140.06) * mm, "mid": v(741.23, 163.83) * mm, "end": v(735.02, 140.06) * mm});
            skPoint(sketch, "E55.centerSnap0", {"position": v(741.23, 163.83) * mm});
            skLineSegment(sketch, "E56.bottom", {"start": v(735.02, 138.43) * mm, "end": v(719, 138.43) * mm});
            skLineSegment(sketch, "E57.bottom", {"start": v(747.45, 138.43) * mm, "end": v(763.46, 138.43) * mm});
            skLineSegment(sketch, "E58", {"start": v(719, 138.43) * mm, "end": v(735.66, 11.43) * mm});
            skLineSegment(sketch, "E59", {"start": v(735.66, 11.43) * mm, "end": v(746.8, 11.43) * mm});
            skLineSegment(sketch, "E60", {"start": v(746.8, 11.43) * mm, "end": v(763.46, 138.43) * mm});
            skLineSegment(sketch, "E61", {"start": v(741.23, 11.43) * mm, "end": v(741.23, 138.43) * mm, "construction": true});
            skLineSegment(sketch, "E62.bottom", {"start": v(719, 163.83) * mm, "end": v(763.46, 163.83) * mm});
            skLineSegment(sketch, "E62.top", {"start": v(719, 11.43) * mm, "end": v(763.46, 11.43) * mm});
            skLineSegment(sketch, "E62.left", {"start": v(719, 163.83) * mm, "end": v(719, 11.43) * mm});
            skLineSegment(sketch, "E62.right", {"start": v(763.46, 163.83) * mm, "end": v(763.46, 11.43) * mm});
            skLineSegment(sketch, "E63", {"start": v(735.02, 140.06) * mm, "end": v(735.02, 138.43) * mm});
            skLineSegment(sketch, "E64", {"start": v(747.45, 140.06) * mm, "end": v(747.45, 138.43) * mm});
            skLineSegment(sketch, "E65", {"start": v(735.02, 140.06) * mm, "end": v(747.45, 140.06) * mm, "construction": true});
            skLineSegment(sketch, "E66", {"start": v(741.23, 140.06) * mm, "end": v(741.23, 134.05) * mm, "construction": true});
            skPoint(sketch, "E67.orphan", {"position": v(741.23, 138.43) * mm});
            skSolve(sketch);
        }
        {
            var Q0;
            {var subQ0=sQuery(id+"F43.wireOp",EDGE,"E57.bottom");Q0=makeQuery(id+"F43.imprint","IMPRINT",FACE,{"disambiguationData":[TD([[makeQuery(id+"F43.imprint","IMPRINT",EDGE,{"derivedFrom":subQ0}),1.0]])]});}
            var Q1;
            {var subQ0=sQuery(id+"F43.wireOp",EDGE,"E56.bottom");Q1=makeQuery(id+"F43.imprint","IMPRINT",FACE,{"disambiguationData":[TD([[makeQuery(id+"F43.imprint","IMPRINT",EDGE,{"derivedFrom":subQ0}),-1.0]])]});}
            var Q2;
            {var subQ0=sQuery(id+"F43.wireOp",EDGE,"E58");Q2=makeQuery(id+"F43.imprint","IMPRINT",FACE,{"disambiguationData":[TD([[makeQuery(id+"F43.imprint","IMPRINT",EDGE,{"derivedFrom":subQ0}),-1.0]])]});}
            var Q3;
            {var subQ0=sQuery(id+"F43.wireOp",EDGE,"E60");Q3=makeQuery(id+"F43.imprint","IMPRINT",FACE,{"disambiguationData":[TD([[makeQuery(id+"F43.imprint","IMPRINT",EDGE,{"derivedFrom":subQ0}),-1.0]])]});}
            extrude(context, id + "F44", {"entities" : qUnion([Q0, Q1, Q2, Q3]), "operationType" : NewBodyOperationType.REMOVE, "endBound" : BoundingType.UP_TO_NEXT, "oppositeDirection" : true, "depth" : 25.4 * mm});
        }
        {
            var Q0;
            {var subQ4=sQuery(id+"F12.wireOp",EDGE,"E15.left");var subQ5=sQuery(id+"F12.wireOp",EDGE,"E15.top");var subQ6=makeQuery(id+"F13.opExtrude","CAP_FACE",FACE,{"disambiguationData":[OSD([sQuery(id+"F12.wireOp",EDGE,"E15.bottom"),subQ5,subQ4,sQuery(id+"F12.wireOp",EDGE,"E15.right")])],"isStart":true});Q0=makeQuery(id+"F32.boolean.opBoolean","MERGE",FACE,{"derivedFrom":[makeQuery(id+"F17.boolean.opBoolean","SPLIT",FACE,{"disambiguationData":[TD([makeQuery(id+"F1.opExtrude","SWEPT_FACE",FACE,{"disambiguationData":[OSD([sQuery(id+"F0.wireOp",EDGE,"E0.left")])]})])],"derivedFrom":subQ6}),makeQuery(id+"F17.boolean.opBoolean","SPLIT",FACE,{"disambiguationData":[TD([makeQuery(id+"F1.opExtrude","SWEPT_FACE",FACE,{"disambiguationData":[OSD([sQuery(id+"F0.wireOp",EDGE,"E5.right")])]})])],"derivedFrom":subQ6}),makeQuery(id+"F32.opExtrude","CAP_FACE",FACE,{"disambiguationData":[OSD([sQuery(id+"F31.wireOp",EDGE,"E31.bottom"),sQuery(id+"F31.wireOp",EDGE,"E31.top"),sQuery(id+"F31.wireOp",EDGE,"E31.left"),sQuery(id+"F31.wireOp",EDGE,"E32")])],"isStart":false})]});}
            var sketch = newSketch(context, id + "F45", { "sketchPlane" : qUnion([Q0])});
            skPoint(sketch, "E68.0", {"position": v(711.2, 800.1) * mm});
            skLineSegment(sketch, "E69.0", {"start": v(246.38, 579.12) * mm, "end": v(723.9, 579.12) * mm, "construction": true});
            skLineSegment(sketch, "E70.bottom", {"start": v(711.2, 800.1) * mm, "end": v(702.74, 800.1) * mm});
            skLineSegment(sketch, "E70.top", {"start": v(711.2, 791.64) * mm, "end": v(702.74, 791.64) * mm});
            skLineSegment(sketch, "E70.left", {"start": v(711.2, 800.1) * mm, "end": v(711.2, 791.64) * mm});
            skLineSegment(sketch, "E70.right", {"start": v(702.74, 800.1) * mm, "end": v(702.74, 791.64) * mm});
            skLineSegment(sketch, "E71.bottom", {"start": v(711.2, 579.12) * mm, "end": v(702.74, 579.12) * mm});
            skLineSegment(sketch, "E71.top", {"start": v(711.2, 587.58) * mm, "end": v(702.74, 587.58) * mm});
            skLineSegment(sketch, "E71.left", {"start": v(711.2, 579.12) * mm, "end": v(711.2, 587.58) * mm});
            skLineSegment(sketch, "E71.right", {"start": v(702.74, 579.12) * mm, "end": v(702.74, 587.58) * mm});
            skLineSegment(sketch, "E72.1.0.0", {"start": v(330.2, 587.58) * mm, "end": v(321.74, 587.58) * mm});
            skLineSegment(sketch, "E72.1.0.1", {"start": v(321.74, 579.12) * mm, "end": v(321.74, 587.58) * mm});
            skLineSegment(sketch, "E72.1.0.2", {"start": v(330.2, 579.12) * mm, "end": v(321.74, 579.12) * mm});
            skLineSegment(sketch, "E72.1.0.3", {"start": v(330.2, 579.12) * mm, "end": v(330.2, 587.58) * mm});
            skLineSegment(sketch, "E72.1.0.4", {"start": v(330.2, 791.64) * mm, "end": v(321.74, 791.64) * mm});
            skLineSegment(sketch, "E72.1.0.5", {"start": v(330.2, 800.1) * mm, "end": v(330.2, 791.64) * mm});
            skLineSegment(sketch, "E72.1.0.6", {"start": v(330.2, 800.1) * mm, "end": v(321.74, 800.1) * mm});
            skLineSegment(sketch, "E72.1.0.7", {"start": v(321.74, 800.1) * mm, "end": v(321.74, 791.64) * mm});
            skLineSegment(sketch, "E72.direction1", {"start": v(702.74, 579.12) * mm, "end": v(321.74, 579.12) * mm, "construction": true});
            skSolve(sketch);
        }
        {
            var Q0;
            {var subQ35=sQuery(id+"F45.wireOp",EDGE,"E70.top");Q0=makeQuery(id+"F45.imprint","IMPRINT",FACE,{"disambiguationData":[TD([[makeQuery(id+"F45.imprint","IMPRINT",EDGE,{"derivedFrom":subQ35}),1.0]])]});}
            var sketch = newSketch(context, id + "F46", { "sketchPlane" : qUnion([Q0])});
            skPoint(sketch, "E73.0", {"position": v(711.2, 800.1) * mm});
            skPoint(sketch, "E74.0", {"position": v(321.74, 579.12) * mm});
            skLineSegment(sketch, "E75.bottom", {"start": v(711.2, 800.1) * mm, "end": v(321.74, 800.1) * mm});
            skLineSegment(sketch, "E75.top", {"start": v(711.2, 579.12) * mm, "end": v(321.74, 579.12) * mm});
            skLineSegment(sketch, "E75.left", {"start": v(711.2, 800.1) * mm, "end": v(711.2, 579.12) * mm});
            skLineSegment(sketch, "E75.right", {"start": v(321.74, 800.1) * mm, "end": v(321.74, 579.12) * mm});
            skLineSegment(sketch, "E76.0", {"start": v(702.74, 791.64) * mm, "end": v(330.2, 791.64) * mm});
            skLineSegment(sketch, "E76.1", {"start": v(702.74, 791.64) * mm, "end": v(702.74, 587.58) * mm});
            skLineSegment(sketch, "E76.2", {"start": v(702.74, 587.58) * mm, "end": v(330.2, 587.58) * mm});
            skLineSegment(sketch, "E76.3", {"start": v(330.2, 791.64) * mm, "end": v(330.2, 587.58) * mm});
            skSolve(sketch);
        }
        {
            var Q0;
            Q0 = qSketchRegion(id + "F46", true);
            extrude(context, id + "F47", {"entities" : qUnion([Q0]), "depth" : 207.44 * mm, "hasSecondDirection" : true, "secondDirectionOppositeDirection" : false, "secondDirectionDepth" : 203.2 * mm});
        }
        {
            var Q0;
            Q0 = qSketchRegion(id + "F45", true);
            var Q1;
            Q1=makeQuery(id+"F47.opExtrude","CAP_FACE",FACE,{"disambiguationData":[OSD([sQuery(id+"F46.wireOp",EDGE,"E75.bottom"),sQuery(id+"F46.wireOp",EDGE,"E75.top"),sQuery(id+"F46.wireOp",EDGE,"E75.left"),sQuery(id+"F46.wireOp",EDGE,"E75.right"),sQuery(id+"F46.wireOp",EDGE,"E76.0"),sQuery(id+"F46.wireOp",EDGE,"E76.1"),sQuery(id+"F46.wireOp",EDGE,"E76.2"),sQuery(id+"F46.wireOp",EDGE,"E76.3")])],"isStart":true});
            extrude(context, id + "F48", {"entities" : qUnion([Q0]), "operationType" : NewBodyOperationType.ADD, "endBound" : BoundingType.UP_TO_SURFACE, "endBoundEntityFace" : qUnion([Q1]), "depth" : 25.4 * mm});
        }
        {
            var Q0;
            Q0=makeQuery(id+"F47.opExtrude","SWEPT_FACE",FACE,{"disambiguationData":[OSD([sQuery(id+"F46.wireOp",EDGE,"E76.3")])]});
            var sketch = newSketch(context, id + "F49", { "sketchPlane" : qUnion([Q0])});
            skPoint(sketch, "E77.0", {"position": v(579.12, 207.44) * mm});
            skLineSegment(sketch, "E78", {"start": v(579.12, 207.44) * mm, "end": v(579.12, 212.77) * mm});
            skLineSegment(sketch, "E79", {"start": v(800.1, 207.44) * mm, "end": v(800.1, 226.5) * mm});
            skLineSegment(sketch, "E80", {"start": v(800.1, 226.5) * mm, "end": v(579.12, 213.83) * mm});
            skLineSegment(sketch, "E81.0", {"start": v(583.36, 207.44) * mm, "end": v(583.36, 213.01) * mm});
            skLineSegment(sketch, "E81.1", {"start": v(795.86, 225.19) * mm, "end": v(691.73, 219.22) * mm});
            skLineSegment(sketch, "E81.2", {"start": v(795.86, 207.44) * mm, "end": v(795.86, 225.19) * mm});
            skLineSegment(sketch, "E82", {"start": v(579.12, 212.77) * mm, "end": v(574.88, 212.53) * mm});
            skLineSegment(sketch, "E83", {"start": v(574.88, 212.53) * mm, "end": v(574.82, 213.59) * mm});
            skLineSegment(sketch, "E84", {"start": v(574.82, 213.59) * mm, "end": v(579.12, 213.83) * mm});
            skLineSegment(sketch, "E85.bottom", {"start": v(691.73, 207.44) * mm, "end": v(687.49, 207.44) * mm});
            skLineSegment(sketch, "E85.left", {"start": v(691.73, 207.44) * mm, "end": v(691.73, 219.22) * mm});
            skLineSegment(sketch, "E85.right", {"start": v(687.49, 207.44) * mm, "end": v(687.49, 218.98) * mm});
            skPoint(sketch, "E85.middle", {"position": v(689.6, 219.1) * mm});
            skLineSegment(sketch, "E86.trimOffspring", {"start": v(687.49, 218.98) * mm, "end": v(583.36, 213.01) * mm});
            skLineSegment(sketch, "E87", {"start": v(579.12, 207.44) * mm, "end": v(583.36, 207.44) * mm});
            skLineSegment(sketch, "E88", {"start": v(795.86, 207.44) * mm, "end": v(800.1, 207.44) * mm});
            skSolve(sketch);
        }
        {
            var Q0;
            Q0 = qSketchRegion(id + "F49", true);
            var Q1;
            Q1=makeQuery(id+"F48.boolean.opBoolean","MERGE",FACE,{"derivedFrom":[makeQuery(id+"F47.opExtrude","SWEPT_FACE",FACE,{"disambiguationData":[OSD([sQuery(id+"F46.wireOp",EDGE,"E75.left")])]}),makeQuery(id+"F48.opExtrude","SWEPT_FACE",FACE,{"disambiguationData":[OSD([sQuery(id+"F45.wireOp",EDGE,"E70.left")])]}),makeQuery(id+"F48.opExtrude","SWEPT_FACE",FACE,{"disambiguationData":[OSD([sQuery(id+"F45.wireOp",EDGE,"E71.left")])]})]});
            var Q2;
            Q2=makeQuery(id+"F48.boolean.opBoolean","MERGE",FACE,{"derivedFrom":[makeQuery(id+"F47.opExtrude","SWEPT_FACE",FACE,{"disambiguationData":[OSD([sQuery(id+"F46.wireOp",EDGE,"E75.right")])]}),makeQuery(id+"F48.opExtrude","SWEPT_FACE",FACE,{"disambiguationData":[OSD([sQuery(id+"F45.wireOp",EDGE,"E72.1.0.1")])]}),makeQuery(id+"F48.opExtrude","SWEPT_FACE",FACE,{"disambiguationData":[OSD([sQuery(id+"F45.wireOp",EDGE,"E72.1.0.7")])]})]});
            extrude(context, id + "F50", {"entities" : qUnion([Q0]), "operationType" : NewBodyOperationType.ADD, "endBound" : BoundingType.UP_TO_SURFACE, "endBoundEntityFace" : qUnion([Q1]), "depth" : 25.4 * mm, "hasSecondDirection" : true, "secondDirectionBound" : SecondDirectionBoundingType.UP_TO_SURFACE, "secondDirectionOppositeDirection" : true, "secondDirectionBoundEntityFace" : qUnion([Q2]), "secondDirectionDepth" : 25.4 * mm});
        }
    });
